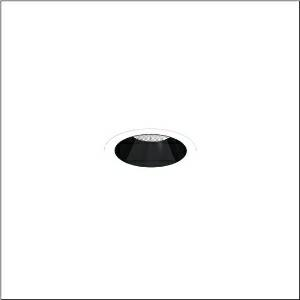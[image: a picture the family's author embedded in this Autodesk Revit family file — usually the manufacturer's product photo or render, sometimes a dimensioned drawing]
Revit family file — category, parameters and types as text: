
# Revit family: lunis_21_m_51db17mc91c
name_source: partatom
category: Lighting Fixtures
units: mm (PartAtom-declared; Revit-internal decimal feet)

## family parameters
Cut with Voids When Loaded = No
Host = Face
Light Source = No
Part Type = Normal
Room Calculation Point = No
Round Connector Dimension = Use Diameter
Shared = No

## types (1)
- --- (1 x LED, 3420 lm, 25.5 W, 6500K)
    Apparent Load = 26 VA
    CIE Flux Codes = 98 100 100 100 100
    Color Rendering = 80
    Color Temperature = 6500K
    Default Elevation = 1800 mm
    Description = Lunis 21 M, downlight, light control with lens, of PMMA, anti glare with reflector, of PC, light emission: direct distribution, LED rated luminous flux: 1.570lm, light colour: 830/840/865, with terminal, 3-pole, mains connection: 220..240V, AC/DC, 0/50..60Hz, housing, round, of diecast aluminium, traffic white (RAL 9016), diameter: 115mm, clamping range: 1..40mm, protection rating (complete): IP20, protection rating (on room side): IP54, insulation class (complete): insulation class II (safety insulation), certification: CE, impact resistance: IK03, packaging unit: 1 piece
    Height = 0 mm  [stored 0 ft]
    Lamp = 1 x LED
    Lamp Light Flux = 3420 lm
    Lamp Power = 25.5 W
    Lamp count = 1
    Length = 115 mm
    Luminous efficacy = 134 lm/W
    Manufacturer = Siteco
    ModVariant = No
    Model = 51DB17MC91C
    Mounting Place = Ceiling
    Mounting Type = Recessed
    Number of Poles = 1
    OnlyDefault = Yes
    Power Factor = 1
    Product Name = Lunis 21 M
    Product group = downlight
    ProductGroupID = 401
    Protection Class = Protection class II
    Protection Degree = IP 20
    RLX_Detail_Level = 1
    RLX_Emergency_Light_Flux = 0 lm
    RLX_Emergency_Type = 0
    RLX_Emergency_Type_DB = No
    RlxData = <blob elided: 15037 chars, md5=d8437fc2>
    Socket = socket
    Standby Power = 0 W
    System Light Flux = 3420 lm
    System Power = 26 W
    Type Comments = individual setting: colour temperature 6500K, luminous flux: 100 % | (ON | ON | OFF | OFF) | 700 mA
    Type Image = l_1290854.jpg
    URL = http://relux.com
    VarID = @adj_035987
    Voltage = 0 V
    Weight = 0.00 kg
    Width = 0 mm  [stored 0 ft]

note: [stored X ft] marks values corroborated as IEEE doubles in the binary element streams (Revit-internal decimal feet)

## geometry (parser evidence)
native form markers: Sweep x11
no freeform markers — native parametric forms only
